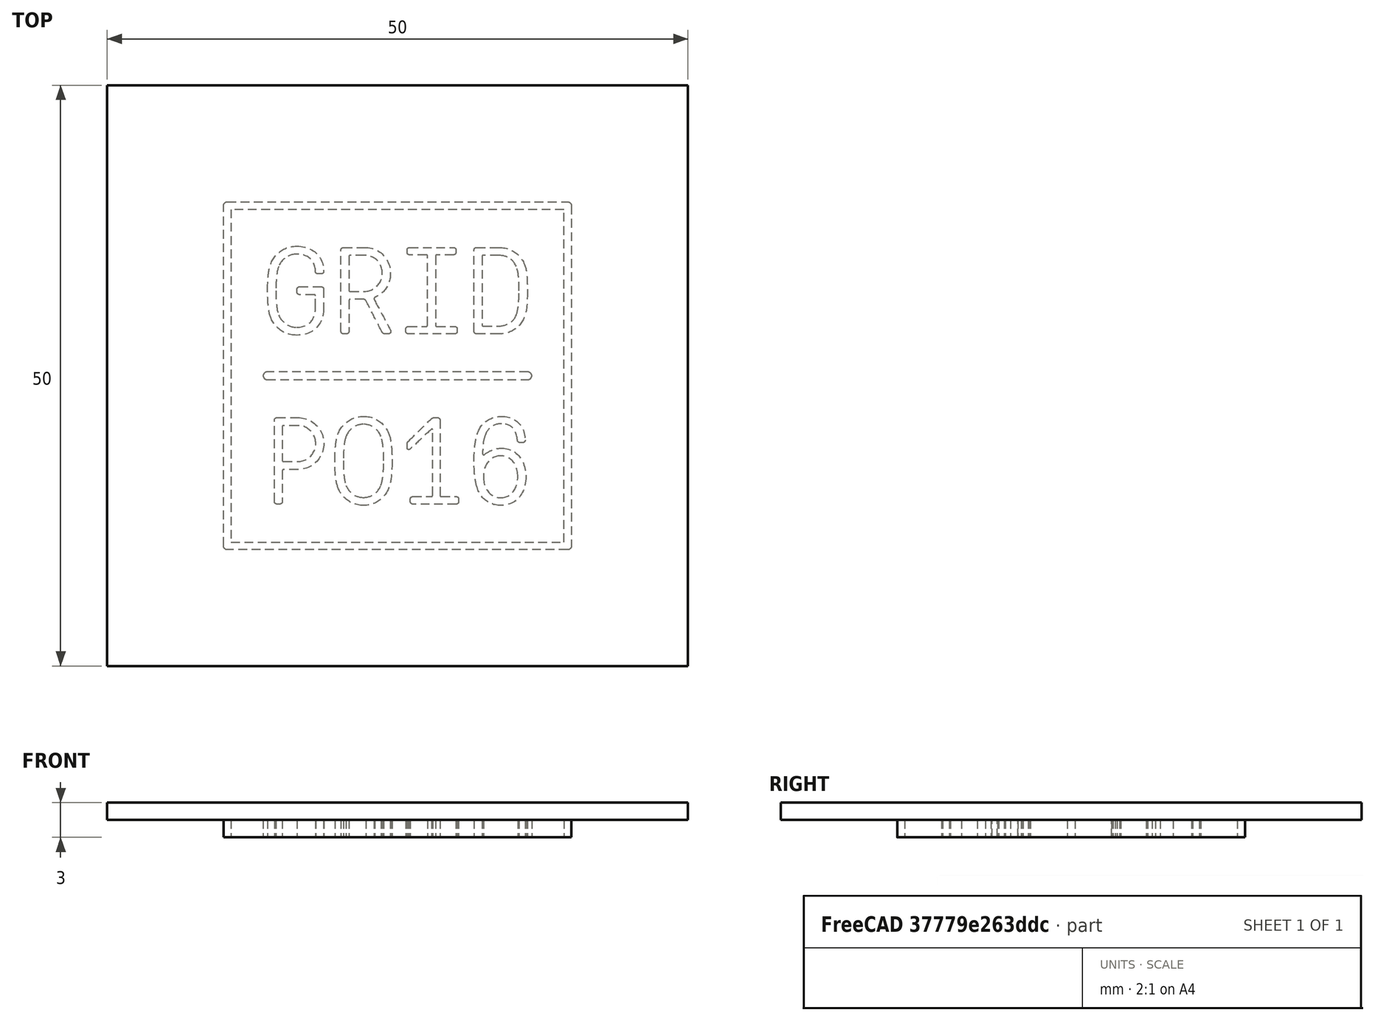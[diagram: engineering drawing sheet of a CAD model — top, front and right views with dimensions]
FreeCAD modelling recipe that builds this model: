
FCSTD DOCUMENT  (FreeCAD 0.18R16131 (Git))
Label: Po16 Logo 5cm
License: All rights reserved
LicenseURL: http://en.wikipedia.org/wiki/All_rights_reserved
objects: Sketcher::SketchObject×3, PartDesign::Pad×3, PartDesign::Body×1
note: 10 computed .brp shape members not serialized (recipe doc carries the construction recipe); baked Part::Feature solids carry a one-line shape summary decoded from their .brp

FEATURE [Sketcher::SketchObject] Sketch016
  sketch-geometry (12):
    g0: BSplineCurve PolesCount=2 KnotsCount=2 Degree=1 IsPeriodic=0
    g1: BSplineCurve PolesCount=4 KnotsCount=2 Degree=3 IsPeriodic=0
    g2: BSplineCurve PolesCount=2 KnotsCount=2 Degree=1 IsPeriodic=0
    g3: BSplineCurve PolesCount=4 KnotsCount=2 Degree=3 IsPeriodic=0
    g4: BSplineCurve PolesCount=2 KnotsCount=2 Degree=1 IsPeriodic=0
    g5: BSplineCurve PolesCount=4 KnotsCount=2 Degree=3 IsPeriodic=0
    g6: BSplineCurve PolesCount=2 KnotsCount=2 Degree=1 IsPeriodic=0
    g7: BSplineCurve PolesCount=4 KnotsCount=2 Degree=3 IsPeriodic=0
    g8: BSplineCurve PolesCount=2 KnotsCount=2 Degree=1 IsPeriodic=0
    g9: BSplineCurve PolesCount=2 KnotsCount=2 Degree=1 IsPeriodic=0
    g10: BSplineCurve PolesCount=2 KnotsCount=2 Degree=1 IsPeriodic=0
    g11: BSplineCurve PolesCount=2 KnotsCount=2 Degree=1 IsPeriodic=0
  constraints (12):
    c: Coincident(g0,g1)
    c: Coincident(g1,g2)
    c: Coincident(g2,g3)
    c: Coincident(g3,g4)
    c: Coincident(g4,g5)
    c: Coincident(g5,g6)
    c: Coincident(g6,g7)
    c: Coincident(g7,g0)
    c: Coincident(g8,g9)
    c: Coincident(g9,g10)
    c: Coincident(g10,g11)
    c: Coincident(g11,g8)
FEATURE [Sketcher::SketchObject] Sketch017
  sketch-geometry (174):
    g0: BSplineCurve PolesCount=2 KnotsCount=2 Degree=1 IsPeriodic=0
    g1: BSplineCurve PolesCount=4 KnotsCount=2 Degree=3 IsPeriodic=0
    g2: BSplineCurve PolesCount=2 KnotsCount=2 Degree=1 IsPeriodic=0
    g3: BSplineCurve PolesCount=4 KnotsCount=2 Degree=3 IsPeriodic=0
    g4: BSplineCurve PolesCount=2 KnotsCount=2 Degree=1 IsPeriodic=0
    g5: BSplineCurve PolesCount=4 KnotsCount=2 Degree=3 IsPeriodic=0
    g6: BSplineCurve PolesCount=2 KnotsCount=2 Degree=1 IsPeriodic=0
    g7: BSplineCurve PolesCount=4 KnotsCount=2 Degree=3 IsPeriodic=0
    g8: BSplineCurve PolesCount=2 KnotsCount=2 Degree=1 IsPeriodic=0
    g9: BSplineCurve PolesCount=4 KnotsCount=2 Degree=3 IsPeriodic=0
    g10: BSplineCurve PolesCount=2 KnotsCount=2 Degree=1 IsPeriodic=0
    g11: BSplineCurve PolesCount=4 KnotsCount=2 Degree=3 IsPeriodic=0
    g12: BSplineCurve PolesCount=2 KnotsCount=2 Degree=1 IsPeriodic=0
    g13: BSplineCurve PolesCount=4 KnotsCount=2 Degree=3 IsPeriodic=0
    g14: BSplineCurve PolesCount=2 KnotsCount=2 Degree=1 IsPeriodic=0
    g15: BSplineCurve PolesCount=4 KnotsCount=2 Degree=3 IsPeriodic=0
    g16: BSplineCurve PolesCount=2 KnotsCount=2 Degree=1 IsPeriodic=0
    g17: BSplineCurve PolesCount=4 KnotsCount=2 Degree=3 IsPeriodic=0
    g18: BSplineCurve PolesCount=2 KnotsCount=2 Degree=1 IsPeriodic=0
    g19: BSplineCurve PolesCount=4 KnotsCount=2 Degree=3 IsPeriodic=0
    g20: BSplineCurve PolesCount=2 KnotsCount=2 Degree=1 IsPeriodic=0
    g21: BSplineCurve PolesCount=4 KnotsCount=2 Degree=3 IsPeriodic=0
    g22: BSplineCurve PolesCount=4 KnotsCount=2 Degree=3 IsPeriodic=0
    g23: BSplineCurve PolesCount=4 KnotsCount=2 Degree=3 IsPeriodic=0
    g24: BSplineCurve PolesCount=4 KnotsCount=2 Degree=3 IsPeriodic=0
    g25: BSplineCurve PolesCount=4 KnotsCount=2 Degree=3 IsPeriodic=0
    g26: BSplineCurve PolesCount=4 KnotsCount=2 Degree=3 IsPeriodic=0
    g27: BSplineCurve PolesCount=2 KnotsCount=2 Degree=1 IsPeriodic=0
    g28: BSplineCurve PolesCount=4 KnotsCount=2 Degree=3 IsPeriodic=0
    g29: BSplineCurve PolesCount=4 KnotsCount=2 Degree=3 IsPeriodic=0
    g30: BSplineCurve PolesCount=4 KnotsCount=2 Degree=3 IsPeriodic=0
    g31: BSplineCurve PolesCount=4 KnotsCount=2 Degree=3 IsPeriodic=0
    g32: BSplineCurve PolesCount=4 KnotsCount=2 Degree=3 IsPeriodic=0
    g33: BSplineCurve PolesCount=4 KnotsCount=2 Degree=3 IsPeriodic=0
    g34: BSplineCurve PolesCount=4 KnotsCount=2 Degree=3 IsPeriodic=0
    g35: BSplineCurve PolesCount=2 KnotsCount=2 Degree=1 IsPeriodic=0
    g36: BSplineCurve PolesCount=4 KnotsCount=2 Degree=3 IsPeriodic=0
    g37: BSplineCurve PolesCount=2 KnotsCount=2 Degree=1 IsPeriodic=0
    g38: BSplineCurve PolesCount=4 KnotsCount=2 Degree=3 IsPeriodic=0
    g39: BSplineCurve PolesCount=2 KnotsCount=2 Degree=1 IsPeriodic=0
    g40: BSplineCurve PolesCount=4 KnotsCount=2 Degree=3 IsPeriodic=0
    g41: BSplineCurve PolesCount=2 KnotsCount=2 Degree=1 IsPeriodic=0
    g42: BSplineCurve PolesCount=4 KnotsCount=2 Degree=3 IsPeriodic=0
    g43: BSplineCurve PolesCount=2 KnotsCount=2 Degree=1 IsPeriodic=0
    g44: BSplineCurve PolesCount=4 KnotsCount=2 Degree=3 IsPeriodic=0
    g45: BSplineCurve PolesCount=4 KnotsCount=2 Degree=3 IsPeriodic=0
    g46: BSplineCurve PolesCount=2 KnotsCount=2 Degree=1 IsPeriodic=0
    g47: BSplineCurve PolesCount=4 KnotsCount=2 Degree=3 IsPeriodic=0
    g48: BSplineCurve PolesCount=2 KnotsCount=2 Degree=1 IsPeriodic=0
    g49: BSplineCurve PolesCount=4 KnotsCount=2 Degree=3 IsPeriodic=0
    g50: BSplineCurve PolesCount=4 KnotsCount=2 Degree=3 IsPeriodic=0
    g51: BSplineCurve PolesCount=4 KnotsCount=2 Degree=3 IsPeriodic=0
    g52: BSplineCurve PolesCount=4 KnotsCount=2 Degree=3 IsPeriodic=0
    g53: BSplineCurve PolesCount=2 KnotsCount=2 Degree=1 IsPeriodic=0
    g54: BSplineCurve PolesCount=4 KnotsCount=2 Degree=3 IsPeriodic=0
    g55: BSplineCurve PolesCount=4 KnotsCount=2 Degree=3 IsPeriodic=0
    g56: BSplineCurve PolesCount=2 KnotsCount=2 Degree=1 IsPeriodic=0
    g57: BSplineCurve PolesCount=4 KnotsCount=2 Degree=3 IsPeriodic=0
    g58: BSplineCurve PolesCount=2 KnotsCount=2 Degree=1 IsPeriodic=0
    g59: BSplineCurve PolesCount=4 KnotsCount=2 Degree=3 IsPeriodic=0
    g60: BSplineCurve PolesCount=2 KnotsCount=2 Degree=1 IsPeriodic=0
    g61: BSplineCurve PolesCount=4 KnotsCount=2 Degree=3 IsPeriodic=0
    g62: BSplineCurve PolesCount=2 KnotsCount=2 Degree=1 IsPeriodic=0
    g63: BSplineCurve PolesCount=4 KnotsCount=2 Degree=3 IsPeriodic=0
    g64: BSplineCurve PolesCount=2 KnotsCount=2 Degree=1 IsPeriodic=0
    g65: BSplineCurve PolesCount=4 KnotsCount=2 Degree=3 IsPeriodic=0
    g66: BSplineCurve PolesCount=4 KnotsCount=2 Degree=3 IsPeriodic=0
    g67: BSplineCurve PolesCount=4 KnotsCount=2 Degree=3 IsPeriodic=0
    g68: BSplineCurve PolesCount=4 KnotsCount=2 Degree=3 IsPeriodic=0
    g69: BSplineCurve PolesCount=2 KnotsCount=2 Degree=1 IsPeriodic=0
    g70: BSplineCurve PolesCount=4 KnotsCount=2 Degree=3 IsPeriodic=0
    g71: BSplineCurve PolesCount=4 KnotsCount=2 Degree=3 IsPeriodic=0
    g72: BSplineCurve PolesCount=2 KnotsCount=2 Degree=1 IsPeriodic=0
    g73: BSplineCurve PolesCount=4 KnotsCount=2 Degree=3 IsPeriodic=0
    g74: BSplineCurve PolesCount=2 KnotsCount=2 Degree=1 IsPeriodic=0
    g75: BSplineCurve PolesCount=4 KnotsCount=2 Degree=3 IsPeriodic=0
    g76: BSplineCurve PolesCount=2 KnotsCount=2 Degree=1 IsPeriodic=0
    g77: BSplineCurve PolesCount=4 KnotsCount=2 Degree=3 IsPeriodic=0
    g78: BSplineCurve PolesCount=2 KnotsCount=2 Degree=1 IsPeriodic=0
    g79: BSplineCurve PolesCount=4 KnotsCount=2 Degree=3 IsPeriodic=0
    g80: BSplineCurve PolesCount=2 KnotsCount=2 Degree=1 IsPeriodic=0
    g81: BSplineCurve PolesCount=4 KnotsCount=2 Degree=3 IsPeriodic=0
    g82: BSplineCurve PolesCount=2 KnotsCount=2 Degree=1 IsPeriodic=0
    g83: BSplineCurve PolesCount=4 KnotsCount=2 Degree=3 IsPeriodic=0
    g84: BSplineCurve PolesCount=2 KnotsCount=2 Degree=1 IsPeriodic=0
    g85: BSplineCurve PolesCount=4 KnotsCount=2 Degree=3 IsPeriodic=0
    g86: BSplineCurve PolesCount=2 KnotsCount=2 Degree=1 IsPeriodic=0
    g87: BSplineCurve PolesCount=4 KnotsCount=2 Degree=3 IsPeriodic=0
    g88: BSplineCurve PolesCount=2 KnotsCount=2 Degree=1 IsPeriodic=0
    g89: BSplineCurve PolesCount=4 KnotsCount=2 Degree=3 IsPeriodic=0
    g90: BSplineCurve PolesCount=2 KnotsCount=2 Degree=1 IsPeriodic=0
    g91: BSplineCurve PolesCount=4 KnotsCount=2 Degree=3 IsPeriodic=0
    g92: BSplineCurve PolesCount=2 KnotsCount=2 Degree=1 IsPeriodic=0
    g93: BSplineCurve PolesCount=4 KnotsCount=2 Degree=3 IsPeriodic=0
    g94: BSplineCurve PolesCount=2 KnotsCount=2 Degree=1 IsPeriodic=0
    g95: BSplineCurve PolesCount=4 KnotsCount=2 Degree=3 IsPeriodic=0
    g96: BSplineCurve PolesCount=2 KnotsCount=2 Degree=1 IsPeriodic=0
    g97: BSplineCurve PolesCount=4 KnotsCount=2 Degree=3 IsPeriodic=0
    g98: BSplineCurve PolesCount=2 KnotsCount=2 Degree=1 IsPeriodic=0
    g99: BSplineCurve PolesCount=4 KnotsCount=2 Degree=3 IsPeriodic=0
    g100: BSplineCurve PolesCount=2 KnotsCount=2 Degree=1 IsPeriodic=0
    g101: BSplineCurve PolesCount=4 KnotsCount=2 Degree=3 IsPeriodic=0
    g102: BSplineCurve PolesCount=2 KnotsCount=2 Degree=1 IsPeriodic=0
    g103: BSplineCurve PolesCount=4 KnotsCount=2 Degree=3 IsPeriodic=0
    g104: BSplineCurve PolesCount=2 KnotsCount=2 Degree=1 IsPeriodic=0
    g105: BSplineCurve PolesCount=4 KnotsCount=2 Degree=3 IsPeriodic=0
    g106: BSplineCurve PolesCount=4 KnotsCount=2 Degree=3 IsPeriodic=0
    g107: BSplineCurve PolesCount=2 KnotsCount=2 Degree=1 IsPeriodic=0
    g108: BSplineCurve PolesCount=4 KnotsCount=2 Degree=3 IsPeriodic=0
    g109: BSplineCurve PolesCount=2 KnotsCount=2 Degree=1 IsPeriodic=0
    g110: BSplineCurve PolesCount=4 KnotsCount=2 Degree=3 IsPeriodic=0
    g111: BSplineCurve PolesCount=2 KnotsCount=2 Degree=1 IsPeriodic=0
    g112: BSplineCurve PolesCount=4 KnotsCount=2 Degree=3 IsPeriodic=0
    g113: BSplineCurve PolesCount=4 KnotsCount=2 Degree=3 IsPeriodic=0
    g114: BSplineCurve PolesCount=4 KnotsCount=2 Degree=3 IsPeriodic=0
    g115: BSplineCurve PolesCount=4 KnotsCount=2 Degree=3 IsPeriodic=0
    g116: BSplineCurve PolesCount=4 KnotsCount=2 Degree=3 IsPeriodic=0
    g117: BSplineCurve PolesCount=4 KnotsCount=2 Degree=3 IsPeriodic=0
    g118: BSplineCurve PolesCount=4 KnotsCount=2 Degree=3 IsPeriodic=0
    g119: BSplineCurve PolesCount=4 KnotsCount=2 Degree=3 IsPeriodic=0
    g120: BSplineCurve PolesCount=4 KnotsCount=2 Degree=3 IsPeriodic=0
    g121: BSplineCurve PolesCount=4 KnotsCount=2 Degree=3 IsPeriodic=0
    g122: BSplineCurve PolesCount=4 KnotsCount=2 Degree=3 IsPeriodic=0
    g123: BSplineCurve PolesCount=4 KnotsCount=2 Degree=3 IsPeriodic=0
    g124: BSplineCurve PolesCount=2 KnotsCount=2 Degree=1 IsPeriodic=0
    g125: BSplineCurve PolesCount=4 KnotsCount=2 Degree=3 IsPeriodic=0
    g126: BSplineCurve PolesCount=2 KnotsCount=2 Degree=1 IsPeriodic=0
    g127: BSplineCurve PolesCount=4 KnotsCount=2 Degree=3 IsPeriodic=0
    g128: BSplineCurve PolesCount=2 KnotsCount=2 Degree=1 IsPeriodic=0
    g129: BSplineCurve PolesCount=4 KnotsCount=2 Degree=3 IsPeriodic=0
    g130: BSplineCurve PolesCount=4 KnotsCount=2 Degree=3 IsPeriodic=0
    g131: BSplineCurve PolesCount=2 KnotsCount=2 Degree=1 IsPeriodic=0
    g132: BSplineCurve PolesCount=4 KnotsCount=2 Degree=3 IsPeriodic=0
    g133: BSplineCurve PolesCount=4 KnotsCount=2 Degree=3 IsPeriodic=0
    g134: BSplineCurve PolesCount=2 KnotsCount=2 Degree=1 IsPeriodic=0
    g135: BSplineCurve PolesCount=4 KnotsCount=2 Degree=3 IsPeriodic=0
    g136: BSplineCurve PolesCount=2 KnotsCount=2 Degree=1 IsPeriodic=0
    g137: BSplineCurve PolesCount=4 KnotsCount=2 Degree=3 IsPeriodic=0
    g138: BSplineCurve PolesCount=2 KnotsCount=2 Degree=1 IsPeriodic=0
    g139: BSplineCurve PolesCount=4 KnotsCount=2 Degree=3 IsPeriodic=0
    g140: BSplineCurve PolesCount=4 KnotsCount=2 Degree=3 IsPeriodic=0
    g141: BSplineCurve PolesCount=2 KnotsCount=2 Degree=1 IsPeriodic=0
    g142: BSplineCurve PolesCount=4 KnotsCount=2 Degree=3 IsPeriodic=0
    g143: BSplineCurve PolesCount=2 KnotsCount=2 Degree=1 IsPeriodic=0
    g144: BSplineCurve PolesCount=4 KnotsCount=2 Degree=3 IsPeriodic=0
    g145: BSplineCurve PolesCount=2 KnotsCount=2 Degree=1 IsPeriodic=0
    g146: BSplineCurve PolesCount=4 KnotsCount=2 Degree=3 IsPeriodic=0
    g147: BSplineCurve PolesCount=4 KnotsCount=2 Degree=3 IsPeriodic=0
    g148: BSplineCurve PolesCount=4 KnotsCount=2 Degree=3 IsPeriodic=0
    g149: BSplineCurve PolesCount=4 KnotsCount=2 Degree=3 IsPeriodic=0
    g150: BSplineCurve PolesCount=4 KnotsCount=2 Degree=3 IsPeriodic=0
    g151: BSplineCurve PolesCount=4 KnotsCount=2 Degree=3 IsPeriodic=0
    g152: BSplineCurve PolesCount=4 KnotsCount=2 Degree=3 IsPeriodic=0
    g153: BSplineCurve PolesCount=4 KnotsCount=2 Degree=3 IsPeriodic=0
    g154: BSplineCurve PolesCount=4 KnotsCount=2 Degree=3 IsPeriodic=0
    g155: BSplineCurve PolesCount=4 KnotsCount=2 Degree=3 IsPeriodic=0
    g156: BSplineCurve PolesCount=4 KnotsCount=2 Degree=3 IsPeriodic=0
    g157: BSplineCurve PolesCount=4 KnotsCount=2 Degree=3 IsPeriodic=0
    g158: BSplineCurve PolesCount=4 KnotsCount=2 Degree=3 IsPeriodic=0
    g159: BSplineCurve PolesCount=4 KnotsCount=2 Degree=3 IsPeriodic=0
    g160: BSplineCurve PolesCount=4 KnotsCount=2 Degree=3 IsPeriodic=0
    g161: BSplineCurve PolesCount=4 KnotsCount=2 Degree=3 IsPeriodic=0
    g162: BSplineCurve PolesCount=4 KnotsCount=2 Degree=3 IsPeriodic=0
    g163: BSplineCurve PolesCount=4 KnotsCount=2 Degree=3 IsPeriodic=0
    g164: BSplineCurve PolesCount=2 KnotsCount=2 Degree=1 IsPeriodic=0
    g165: BSplineCurve PolesCount=4 KnotsCount=2 Degree=3 IsPeriodic=0
    g166: BSplineCurve PolesCount=4 KnotsCount=2 Degree=3 IsPeriodic=0
    g167: BSplineCurve PolesCount=4 KnotsCount=2 Degree=3 IsPeriodic=0
    g168: BSplineCurve PolesCount=4 KnotsCount=2 Degree=3 IsPeriodic=0
    g169: BSplineCurve PolesCount=4 KnotsCount=2 Degree=3 IsPeriodic=0
    g170: BSplineCurve PolesCount=4 KnotsCount=2 Degree=3 IsPeriodic=0
    g171: BSplineCurve PolesCount=4 KnotsCount=2 Degree=3 IsPeriodic=0
    g172: BSplineCurve PolesCount=4 KnotsCount=2 Degree=3 IsPeriodic=0
    g173: BSplineCurve PolesCount=4 KnotsCount=2 Degree=3 IsPeriodic=0
  constraints (174):
    c: Coincident(g0,g1)
    c: Coincident(g1,g2)
    c: Coincident(g2,g3)
    c: Coincident(g3,g4)
    c: Coincident(g4,g5)
    c: Coincident(g5,g6)
    c: Coincident(g6,g7)
    c: Coincident(g7,g8)
    c: Coincident(g8,g9)
    c: Coincident(g9,g10)
    c: Coincident(g10,g11)
    c: Coincident(g11,g12)
    c: Coincident(g12,g13)
    c: Coincident(g13,g14)
    c: Coincident(g14,g15)
    c: Coincident(g15,g16)
    c: Coincident(g16,g17)
    c: Coincident(g17,g18)
    c: Coincident(g18,g19)
    c: Coincident(g19,g20)
    c: Coincident(g20,g21)
    c: Coincident(g21,g0)
    c: Coincident(g22,g23)
    c: Coincident(g23,g24)
    c: Coincident(g24,g25)
    c: Coincident(g25,g26)
    c: Coincident(g26,g27)
    c: Coincident(g27,g28)
    c: Coincident(g28,g29)
    c: Coincident(g29,g30)
    c: Coincident(g30,g31)
    c: Coincident(g31,g32)
    c: Coincident(g32,g33)
    c: Coincident(g33,g34)
    c: Coincident(g34,g35)
    c: Coincident(g35,g36)
    c: Coincident(g36,g37)
    c: Coincident(g37,g38)
    c: Coincident(g38,g39)
    c: Coincident(g39,g40)
    c: Coincident(g40,g41)
    c: Coincident(g41,g42)
    c: Coincident(g42,g43)
    c: Coincident(g43,g44)
    c: Coincident(g44,g45)
    c: Coincident(g45,g22)
    c: Coincident(g46,g47)
    c: Coincident(g47,g48)
    c: Coincident(g48,g49)
    c: Coincident(g49,g50)
    c: Coincident(g50,g51)
    c: Coincident(g51,g52)
    c: Coincident(g52,g53)
    c: Coincident(g53,g54)
    c: Coincident(g54,g46)
    c: Coincident(g55,g56)
    c: Coincident(g56,g57)
    c: Coincident(g57,g58)
    c: Coincident(g58,g59)
    c: Coincident(g59,g60)
    c: Coincident(g60,g61)
    c: Coincident(g61,g55)
    c: Coincident(g62,g63)
    c: Coincident(g63,g64)
    c: Coincident(g64,g65)
    c: Coincident(g65,g66)
    c: Coincident(g66,g67)
    c: Coincident(g67,g68)
    c: Coincident(g68,g69)
    c: Coincident(g69,g70)
    c: Coincident(g70,g71)
    c: Coincident(g71,g72)
    c: Coincident(g72,g73)
    c: Coincident(g73,g74)
    c: Coincident(g74,g75)
    c: Coincident(g75,g76)
    c: Coincident(g76,g77)
    c: Coincident(g77,g78)
    c: Coincident(g78,g79)
    c: Coincident(g79,g80)
    c: Coincident(g80,g81)
    c: Coincident(g81,g62)
    c: Coincident(g82,g83)
    c: Coincident(g83,g84)
    c: Coincident(g84,g85)
    c: Coincident(g85,g86)
    c: Coincident(g86,g87)
    c: Coincident(g87,g88)
    c: Coincident(g88,g89)
    c: Coincident(g89,g90)
    c: Coincident(g90,g91)
    c: Coincident(g91,g92)
    c: Coincident(g92,g93)
    c: Coincident(g93,g94)
    c: Coincident(g94,g95)
    c: Coincident(g95,g96)
    c: Coincident(g96,g97)
    c: Coincident(g97,g98)
    c: Coincident(g98,g99)
    c: Coincident(g99,g100)
    c: Coincident(g100,g101)
    c: Coincident(g101,g102)
    c: Coincident(g102,g103)
    c: Coincident(g103,g104)
    c: Coincident(g104,g105)
    c: Coincident(g105,g82)
    c: Coincident(g106,g107)
    c: Coincident(g107,g108)
    c: Coincident(g108,g109)
    c: Coincident(g109,g110)
    c: Coincident(g110,g111)
    c: Coincident(g111,g112)
    c: Coincident(g112,g106)
    c: Coincident(g113,g114)
    c: Coincident(g114,g115)
    c: Coincident(g115,g116)
    c: Coincident(g116,g117)
    c: Coincident(g117,g118)
    c: Coincident(g118,g119)
    c: Coincident(g119,g120)
    c: Coincident(g120,g113)
    c: Coincident(g121,g122)
    c: Coincident(g122,g123)
    c: Coincident(g123,g124)
    c: Coincident(g124,g125)
    c: Coincident(g125,g126)
    c: Coincident(g126,g127)
    c: Coincident(g127,g128)
    c: Coincident(g128,g129)
    c: Coincident(g129,g121)
    c: Coincident(g130,g131)
    c: Coincident(g131,g132)
    c: Coincident(g132,g133)
    c: Coincident(g133,g134)
    c: Coincident(g134,g135)
    c: Coincident(g135,g130)
    c: Coincident(g136,g137)
    c: Coincident(g137,g138)
    c: Coincident(g138,g139)
    c: Coincident(g139,g140)
    c: Coincident(g140,g141)
    c: Coincident(g141,g142)
    c: Coincident(g142,g143)
    c: Coincident(g143,g144)
    c: Coincident(g144,g145)
    c: Coincident(g145,g146)
    c: Coincident(g146,g136)
    c: Coincident(g147,g148)
    c: Coincident(g148,g149)
    c: Coincident(g149,g150)
    c: Coincident(g150,g147)
    c: Coincident(g151,g152)
    c: Coincident(g152,g153)
    c: Coincident(g153,g154)
    c: Coincident(g154,g155)
    c: Coincident(g155,g156)
    c: Coincident(g156,g157)
    c: Coincident(g157,g158)
    c: Coincident(g158,g151)
    c: Coincident(g159,g160)
    c: Coincident(g160,g161)
    c: Coincident(g161,g162)
    c: Coincident(g162,g163)
    c: Coincident(g163,g164)
    c: Coincident(g164,g165)
    c: Coincident(g165,g166)
    c: Coincident(g166,g167)
    c: Coincident(g167,g168)
    c: Coincident(g168,g169)
    c: Coincident(g169,g170)
    c: Coincident(g170,g171)
    c: Coincident(g171,g172)
    c: Coincident(g172,g173)
    c: Coincident(g173,g159)
FEATURE [Sketcher::SketchObject] Sketch
  MapMode = 5
  Support = -> [XY_Plane]
  sketch-geometry (5):
    g0: LineSegment StartX=-25 StartY=25 StartZ=0 EndX=-25 EndY=-25 EndZ=0
    g1: LineSegment StartX=-25 StartY=-25 StartZ=0 EndX=25 EndY=-25 EndZ=0
    g2: LineSegment StartX=25 StartY=-25 StartZ=0 EndX=25 EndY=25 EndZ=0
    g3: LineSegment StartX=25 StartY=25 StartZ=0 EndX=-25 EndY=25 EndZ=0
    g4: Circle [constr] CenterX=0 CenterY=0 CenterZ=0 NormalX=0 NormalY=0 NormalZ=1 AngleXU=0 Radius=35.3553
  constraints (14):
    c: Coincident(g0,g1)
    c: Coincident(g1,g2)
    c: Coincident(g2,g3)
    c: Coincident(g3,g0)
    c: Equal(g0,g1)
    c: Equal(g0,g2)
    c: Equal(g0,g3)
    c: PointOnObject(g0,g4)
    c: PointOnObject(g1,g4)
    c: PointOnObject(g2,g4)
    c: PointOnObject(g3,g4)
    c: Coincident(g4,g-1)
    c: Horizontal(g3)
    c: DistanceX(g3,g3) = 50
FEATURE [PartDesign::Pad] Pad
  Length = 1.5
  Length2 = 100
  Profile = -> Sketch
  Type = 0
FEATURE [PartDesign::Pad] Pad001
  BaseFeature = -> Pad
  Length = 1.5
  Length2 = 100
  Profile = -> Sketch016
  Reversed = true
  Type = 0
FEATURE [PartDesign::Pad] Pad002
  BaseFeature = -> Pad001
  Length = 1.5
  Length2 = 100
  Profile = -> Sketch017
  Reversed = true
  Type = 0
FEATURE [PartDesign::Body] Body
  Group = -> [Sketch,Pad,Sketch016,Sketch017,Pad001,Pad002]
  Origin = -> Origin
  Tip = -> Pad002
